FCSTD DOCUMENT
Label: Resistor
objects: Sketcher::SketchObject×1
note: 1 computed .brp shape members not serialized (recipe doc carries the construction recipe); baked Part::Feature solids carry a one-line shape summary decoded from their .brp

FEATURE [Sketcher::SketchObject] Sketch
  Placement = pos=(0,0,0) rot=(-1,0,0;4.71239rad)
  sketch-geometry (11):
    g0: LineSegment StartX=10.2196 StartY=39.9084 StartZ=0 EndX=21.2973 EndY=39.9084 EndZ=0
    g1: LineSegment StartX=21.2973 StartY=39.9084 StartZ=0 EndX=22.1691 EndY=42.8645 EndZ=0
    g2: LineSegment StartX=22.1691 StartY=42.8645 StartZ=0 EndX=24.7803 EndY=38.069 EndZ=0
    g3: LineSegment StartX=24.7803 StartY=38.069 StartZ=0 EndX=26.1946 EndY=42.8645 EndZ=0
    g4: LineSegment StartX=26.1946 StartY=42.8645 StartZ=0 EndX=28.8057 EndY=38.069 EndZ=0
    g5: LineSegment StartX=28.8057 StartY=38.069 StartZ=0 EndX=30.3694 EndY=42.8645 EndZ=0
    g6: LineSegment StartX=30.3694 StartY=42.8645 StartZ=0 EndX=31.832 EndY=39.9866 EndZ=0
    g7: LineSegment StartX=31.832 StartY=39.9866 StartZ=0 EndX=42.9097 EndY=39.9866 EndZ=0
    g8: LineSegment [constr] StartX=22.1691 StartY=42.8645 StartZ=0 EndX=26.1946 EndY=42.8645 EndZ=0
    g9: LineSegment [constr] StartX=26.1946 StartY=42.8645 StartZ=0 EndX=30.3694 EndY=42.8645 EndZ=0
    g10: LineSegment [constr] StartX=24.7803 StartY=38.069 StartZ=0 EndX=28.8057 EndY=38.069 EndZ=0
  constraints (23):
    c: Horizontal(g0)
    c: Coincident(g0,g1)
    c: Coincident(g1,g2)
    c: Coincident(g2,g3)
    c: Coincident(g3,g4)
    c: Coincident(g4,g5)
    c: Coincident(g5,g6)
    c: Coincident(g6,g7)
    c: Horizontal(g7)
    c: Angle(g1,g2) = 0.785398
    c: Angle(g3,g2) = 0.785398
    c: Coincident(g8,g1)
    c: Coincident(g8,g3)
    c: Horizontal(g8)
    c: Coincident(g9,g3)
    c: Coincident(g9,g5)
    c: Horizontal(g9)
    c: Coincident(g10,g2)
    c: Coincident(g10,g4)
    c: Horizontal(g10)
    c: Angle(g3,g4) = 0.785398
    c: Angle(g5,g6) = 0.785398
    c: Equal(g0,g7)
